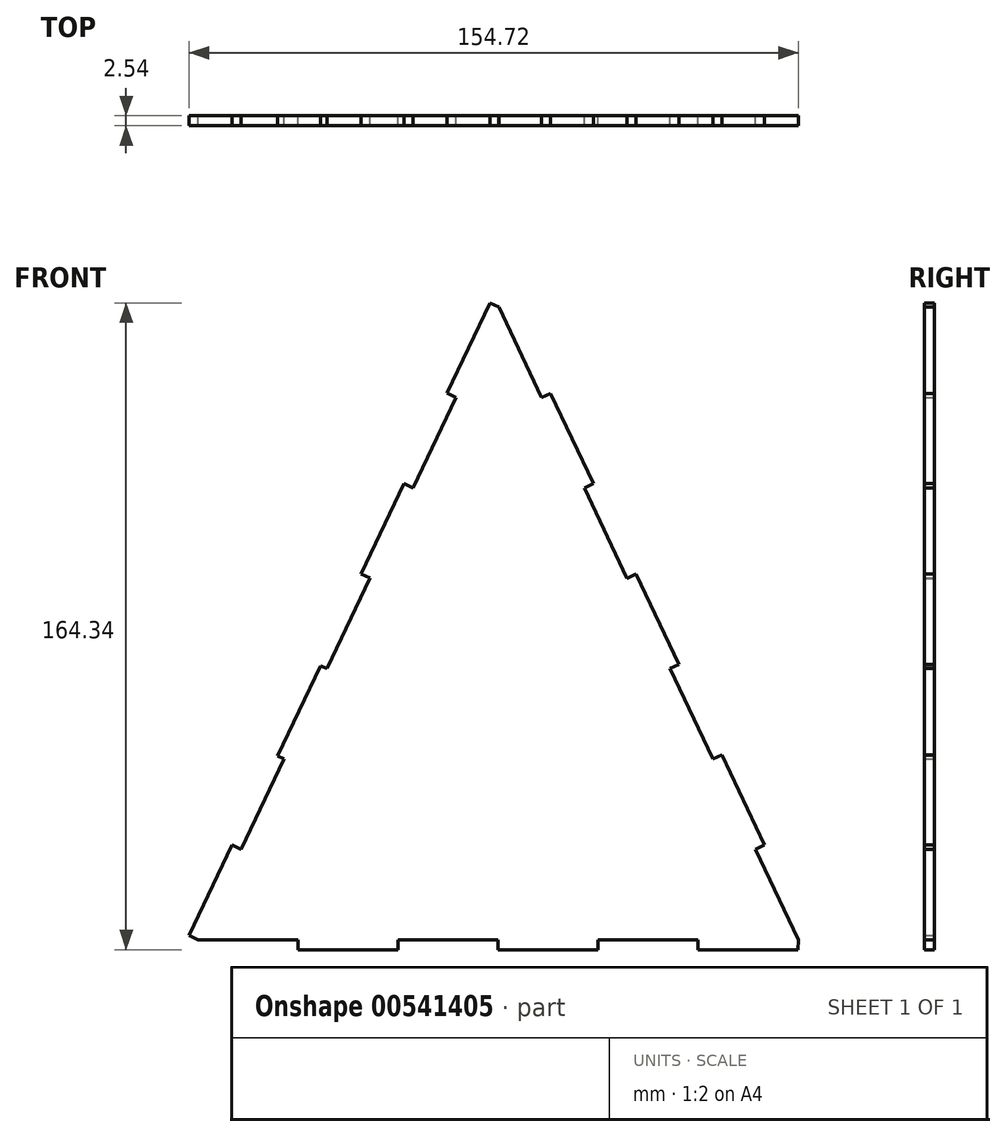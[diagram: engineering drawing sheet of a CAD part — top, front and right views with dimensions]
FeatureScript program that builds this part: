
annotation { "Feature Type Name" : "Feature", "Feature Type Description" : "" }
export const myFeature = defineFeature(function(context is Context, id is Id, definition is map)
    precondition{}
    {
        {
            var Q0;
            Q0=qCreatedBy(makeId("Front.planeOp"),FACE);
            var sketch = newSketch(context, id + "F0", { "sketchPlane" : qUnion([Q0])});
            skLineSegment(sketch, "E0", {"start": v(-10.9, 63.99) * mm, "end": v(-54.56, -27.9) * mm});
            skLineSegment(sketch, "E1", {"start": v(-76.36, -73.78) * mm, "end": v(76.06, -73.78) * mm});
            skLineSegment(sketch, "E2", {"start": v(76.06, -73.78) * mm, "end": v(0, 86.93) * mm});
            skLineSegment(sketch, "E3", {"start": v(0, 86.93) * mm, "end": v(-2.3, 88.02) * mm});
            skLineSegment(sketch, "E4", {"start": v(-2.3, 88.02) * mm, "end": v(-13.2, 65.08) * mm});
            skLineSegment(sketch, "E5", {"start": v(-13.2, 65.08) * mm, "end": v(-10.9, 63.99) * mm});
            skLineSegment(sketch, "E6", {"start": v(-24.1, 42.14) * mm, "end": v(-35, 19.2) * mm});
            skLineSegment(sketch, "E7", {"start": v(-35, 19.2) * mm, "end": v(-32.7, 18.1) * mm});
            skLineSegment(sketch, "E8", {"start": v(-43.6, -4.84) * mm, "end": v(-45.27, -4.19) * mm});
            skLineSegment(sketch, "E9", {"start": v(-45.27, -4.19) * mm, "end": v(-56.17, -27.13) * mm});
            skLineSegment(sketch, "E10", {"start": v(-56.17, -27.13) * mm, "end": v(-54.56, -27.9) * mm});
            skLineSegment(sketch, "E11", {"start": v(-54.56, -27.9) * mm, "end": v(-65.46, -50.84) * mm});
            skLineSegment(sketch, "E12", {"start": v(-65.46, -50.84) * mm, "end": v(-67.76, -49.75) * mm});
            skLineSegment(sketch, "E13", {"start": v(-67.76, -49.75) * mm, "end": v(-78.66, -72.7) * mm});
            skLineSegment(sketch, "E14", {"start": v(-78.66, -72.7) * mm, "end": v(-76.36, -73.78) * mm});
            skLineSegment(sketch, "E15", {"start": v(-76.36, -73.78) * mm, "end": v(-50.96, -73.78) * mm});
            skLineSegment(sketch, "E16", {"start": v(-50.96, -73.78) * mm, "end": v(-50.96, -76.32) * mm});
            skLineSegment(sketch, "E17", {"start": v(-50.96, -76.32) * mm, "end": v(-25.56, -76.32) * mm});
            skLineSegment(sketch, "E18", {"start": v(-25.56, -76.32) * mm, "end": v(-25.56, -73.78) * mm});
            skLineSegment(sketch, "E19", {"start": v(-25.56, -73.78) * mm, "end": v(-0.15, -73.78) * mm});
            skLineSegment(sketch, "E20", {"start": v(-0.15, -73.78) * mm, "end": v(-0.15, -76.32) * mm});
            skLineSegment(sketch, "E21", {"start": v(-0.15, -76.32) * mm, "end": v(25.25, -76.32) * mm});
            skLineSegment(sketch, "E22", {"start": v(25.25, -76.32) * mm, "end": v(25.25, -73.78) * mm});
            skLineSegment(sketch, "E23", {"start": v(25.25, -73.78) * mm, "end": v(50.65, -73.78) * mm});
            skLineSegment(sketch, "E24", {"start": v(50.65, -73.78) * mm, "end": v(50.65, -76.32) * mm});
            skPoint(sketch, "E25", {"position": v(78.35, 9.9) * mm});
            skLineSegment(sketch, "E26", {"start": v(50.65, -76.32) * mm, "end": v(76.05, -76.32) * mm});
            skLineSegment(sketch, "E27", {"start": v(76.05, -76.32) * mm, "end": v(76.06, -73.78) * mm});
            skLineSegment(sketch, "E28", {"start": v(76.06, -73.78) * mm, "end": v(65.2, -50.82) * mm});
            skLineSegment(sketch, "E29", {"start": v(65.2, -50.82) * mm, "end": v(67.5, -49.74) * mm});
            skLineSegment(sketch, "E30", {"start": v(67.5, -49.74) * mm, "end": v(56.62, -26.78) * mm});
            skLineSegment(sketch, "E31", {"start": v(56.62, -26.78) * mm, "end": v(54.33, -27.86) * mm});
            skLineSegment(sketch, "E32", {"start": v(43.46, -4.9) * mm, "end": v(45.76, -3.82) * mm});
            skLineSegment(sketch, "E33", {"start": v(45.76, -3.82) * mm, "end": v(34.9, 19.14) * mm});
            skLineSegment(sketch, "E34", {"start": v(34.9, 19.14) * mm, "end": v(32.6, 18.05) * mm});
            skLineSegment(sketch, "E35", {"start": v(21.73, 41.01) * mm, "end": v(24.03, 42.1) * mm});
            skLineSegment(sketch, "E36", {"start": v(24.03, 42.1) * mm, "end": v(13.16, 65.06) * mm});
            skLineSegment(sketch, "E37", {"start": v(13.16, 65.06) * mm, "end": v(10.87, 63.97) * mm});
            skLineSegment(sketch, "E38.trimOffspring", {"start": v(-65.46, -50.84) * mm, "end": v(-76.36, -73.78) * mm});
            skLineSegment(sketch, "E39", {"start": v(0, 86.93) * mm, "end": v(-10.9, 63.99) * mm});
            skLineSegment(sketch, "E40", {"start": v(-24.1, 42.14) * mm, "end": v(-21.8, 41.05) * mm});
            skSolve(sketch);
        }
        {
            var Q0;
            Q0=qSketchRegion(id+"F0",true);
            extrude(context, id + "F1", {"entities" : qUnion([Q0]), "depth" : 2.54 * mm, "offsetDistance" : 25.4 * mm});
        }
        {
            var Q0;
            Q0=qSketchRegion(id+"F0",true);
            extrude(context, id + "F2", {"entities" : qUnion([Q0]), "operationType" : NewBodyOperationType.ADD, "depth" : 2.54 * mm, "offsetDistance" : 25.4 * mm});
        }
    });
